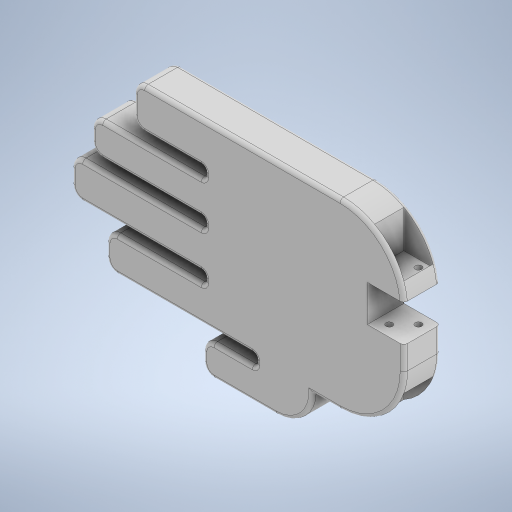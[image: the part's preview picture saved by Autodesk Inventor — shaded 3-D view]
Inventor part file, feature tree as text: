
AUTODESK INVENTOR PART (.ipt)
format: ipt  version: 2024 (Build 280153000, 153)  size: 504,320 bytes
history: native  units: mm
features: extrude x10, fillet x4, sketch x3, plane x2, revolve x1, hole x1
ambient origin geometry x8: Origin, YZ Plane, XZ Plane, XY Plane, X Axis, Y Axis, Z Axis, Center Point
bodies: Solid1 (feature_tree)
feature tree (21):
  extrude  "Extrusion1"  Depth=95.0mm
  extrude  "Extrusion2"  Depth=20.0mm
  extrude  "Extrusion3"  Depth=2.0mm
  extrude  "Extrusion4"  Depth=2.0mm
  extrude  "Extrusion5"  Depth=10.0mm
  fillet  "Fillet1"  Radius=27.0mm
  plane  "Work Plane3"
  plane  "Work Plane4"
  extrude  "Extrusion10"  Depth=2.0mm
  revolve  "Revolution7"  [1 undecoded]
  extrude  "Extrusion14"  Depth=2.0mm TaperAngle=0.0deg
  extrude  "Extrusion15"  Depth=2.0mm TaperAngle=0.0deg
  sketch  "Sketch26"  dims[d2=20.0mm d3=0.0mm d4=20.0mm]
  extrude  "Extrusion16"  Depth=2.0mm TaperAngle=0.0deg
  hole  "Hole1"  [1 undecoded]
  extrude  "Extrusion17"  Depth=2.0mm
  fillet  "Fillet17"  [1 undecoded]
  fillet  "Fillet18"  Radius=20.0mm
  fillet  "Fillet19"  Radius=20.0mm
  sketch  "Sketch25"  dims[d0=100.0mm d1=95.0mm]
  sketch  "Sketch27"  dims[d5=20.0mm d6=20.0mm d7=20.0mm d8=10.0mm d10=27.0mm d11=27.0mm d12=53.0mm d13=0.0mm d14=76.0mm d15=0.0mm d16=87.0mm d17=0.0mm d18=68.0mm d19=0.0mm d40=35.0mm d45=65.0mm d62=-70.0mm d63=20.0mm d64=20.0mm d65=40.0mm d66=0.0mm d67=90.0deg d98=20.0mm d99=20.0mm d100=48.0mm d101=20.0mm d102=20.0mm d103=0.0mm d104=20.0mm d105=20.0mm d106=25.0mm d107=0.0mm d108=20.0mm d109=20.0mm d110=40.0mm d111=0.0mm d112=8.0mm d113=8.0mm d114=6.0mm d115=6.0mm d116=3.6mm d117=6.0mm d118=6.3mm d119=2.0mm d120=90.0deg d121=8.0mm d122=20.594885mm d123=0.0mm d124=0.0mm d125=6.0mm d126=2.0mm d127=2.0mm d41=0.0mm d42=0.0mm d43=0.0mm]
note: 3 required parameter values undecoded (feature->parameter linkage not recoverable at this tier; creation-order binding heuristic only, values carry confidence <= 0.55)